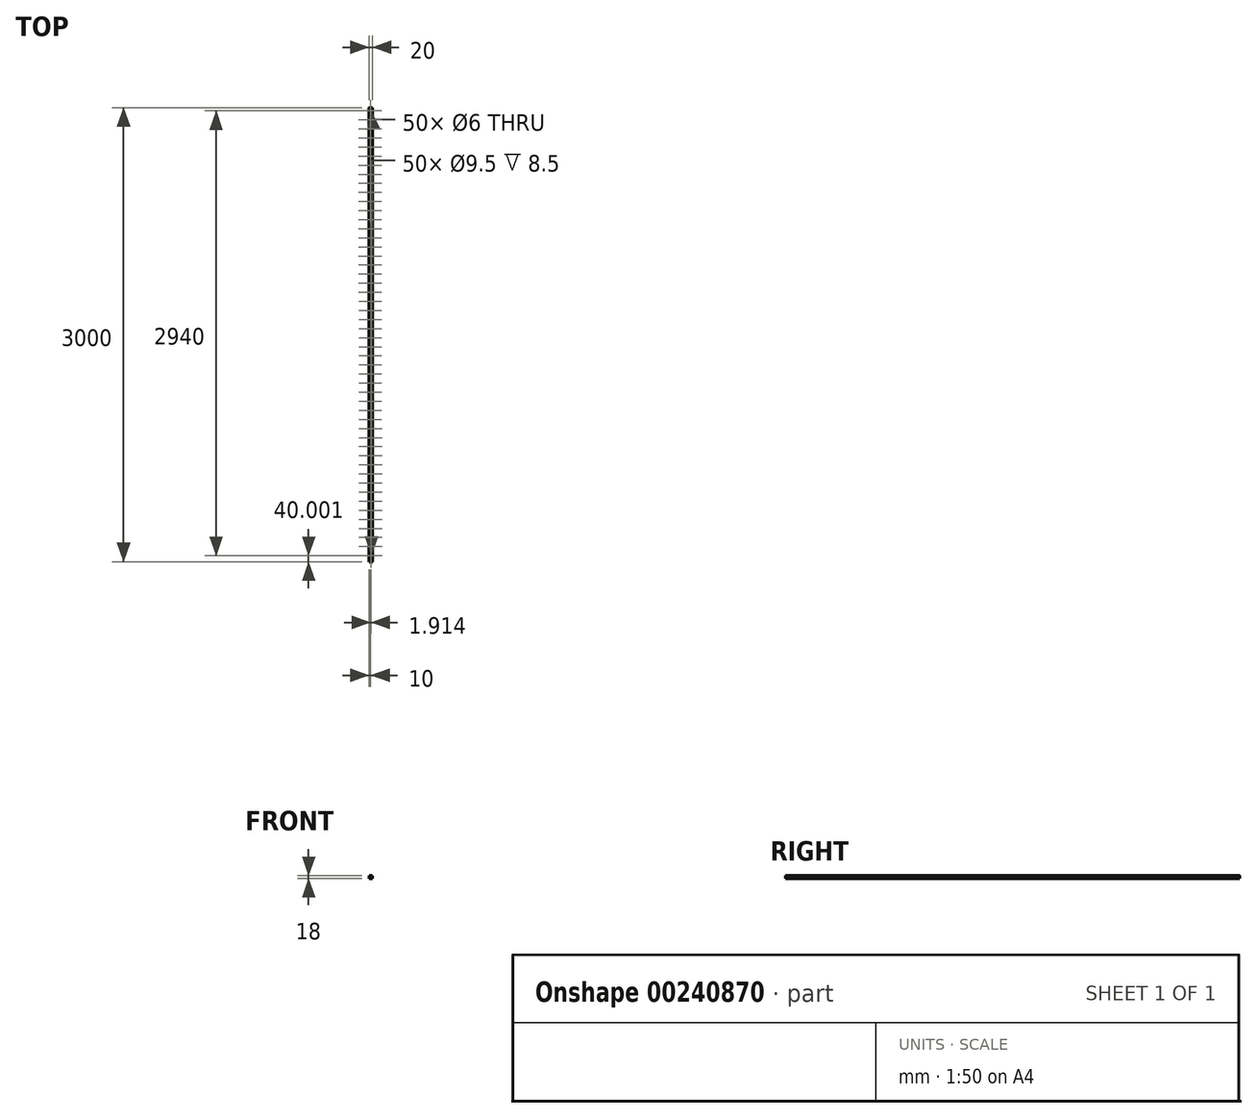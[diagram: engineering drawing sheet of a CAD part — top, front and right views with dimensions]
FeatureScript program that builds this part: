
annotation { "Feature Type Name" : "Feature", "Feature Type Description" : "" }
export const myFeature = defineFeature(function(context is Context, id is Id, definition is map)
    precondition{}
    {
        {
            var Q0;
            Q0=qCreatedBy(makeId("Front.planeOp"),FACE);
            var sketch = newSketch(context, id + "F0", { "sketchPlane" : qUnion([Q0])});
            skLineSegment(sketch, "E0.bottom", {"start": v(-10, 0) * mm, "end": v(10, 0) * mm});
            skLineSegment(sketch, "E0.top", {"start": v(-10, 18) * mm, "end": v(10, 18) * mm});
            skLineSegment(sketch, "E0.left", {"start": v(-10, 0) * mm, "end": v(-10, 18) * mm});
            skLineSegment(sketch, "E0.right", {"start": v(10, 0) * mm, "end": v(10, 18) * mm});
            skLineSegment(sketch, "E1", {"start": v(-18.81, 15) * mm, "end": v(15.35, 15) * mm, "construction": true});
            skCircle(sketch, "E2", {"center": v(-10, 18) * mm, "radius": 2 * mm});
            skCircle(sketch, "E3", {"center": v(10, 18) * mm, "radius": 2 * mm});
            skLineSegment(sketch, "E4.rect.bottom", {"start": v(-2, 0.5) * mm, "end": v(2, 0.5) * mm});
            skLineSegment(sketch, "E4.rect.top", {"start": v(-2, -0.5) * mm, "end": v(2, -0.5) * mm});
            skLineSegment(sketch, "E4.rect.left", {"start": v(-2, 0.5) * mm, "end": v(-2, -0.5) * mm});
            skLineSegment(sketch, "E4.rect.right", {"start": v(2, 0.5) * mm, "end": v(2, -0.5) * mm});
            skPoint(sketch, "E4.rect.middle", {"position": v(0, 0) * mm});
            skCircle(sketch, "E5.MirrorC", {"center": v(-10, 12) * mm, "radius": 2 * mm});
            skCircle(sketch, "E6.MirrorC", {"center": v(10, 12) * mm, "radius": 2 * mm});
            skLineSegment(sketch, "E7", {"start": v(-10, 0.42) * mm, "end": v(-9.58, 0) * mm});
            skLineSegment(sketch, "E8", {"start": v(-13.72, 4) * mm, "end": v(14.81, 4) * mm, "construction": true});
            skLineSegment(sketch, "E9", {"start": v(-12.78, 5.46) * mm, "end": v(14.15, 5.46) * mm, "construction": true});
            skLineSegment(sketch, "E10", {"start": v(-12.88, 2.54) * mm, "end": v(14.15, 2.54) * mm, "construction": true});
            skLineSegment(sketch, "E11", {"start": v(-9.79, 0.21) * mm, "end": v(-10, 0) * mm, "construction": true});
            skLineSegment(sketch, "E12.MirrorCS", {"start": v(10, 0.42) * mm, "end": v(9.58, 0) * mm});
            skCircle(sketch, "E13", {"center": v(-7, 0) * mm, "radius": 0.5 * mm});
            skLineSegment(sketch, "E14", {"start": v(-2, 0.5) * mm, "end": v(-2.5, 0) * mm});
            skLineSegment(sketch, "E15", {"start": v(-2.25, 0.25) * mm, "end": v(-2, 0) * mm, "construction": true});
            skLineSegment(sketch, "E16.MirrorCS", {"start": v(2, 0.5) * mm, "end": v(2.5, 0) * mm});
            skLineSegment(sketch, "E17", {"start": v(-7, 0) * mm, "end": v(-7, 20.38) * mm, "construction": true});
            skLineSegment(sketch, "E18.MirrorCS", {"start": v(7, 0) * mm, "end": v(7, 20.38) * mm, "construction": true});
            skLineSegment(sketch, "E19", {"start": v(-10, 5.46) * mm, "end": v(-7, 8.46) * mm});
            skLineSegment(sketch, "E20", {"start": v(-7, 8.46) * mm, "end": v(-7, 10.93) * mm});
            skLineSegment(sketch, "E21", {"start": v(-7, 10.93) * mm, "end": v(-8.03, 11.65) * mm});
            skLineSegment(sketch, "E22.MirrorCS", {"start": v(10, 5.46) * mm, "end": v(7, 8.46) * mm});
            skLineSegment(sketch, "E23.MirrorCS", {"start": v(7, 8.46) * mm, "end": v(7, 10.93) * mm});
            skLineSegment(sketch, "E24.MirrorCS", {"start": v(7, 10.93) * mm, "end": v(8.03, 11.65) * mm});
            skSolve(sketch);
        }
        {
            var Q0;
            Q0=makeQuery(id+"F0.imprint","IMPRINT",FACE,{"disambiguationData":[TD([[makeQuery(id+"F0.imprint","IMPRINT",EDGE,{"derivedFrom":sQuery(id+"F0.wireOp",EDGE,"E4.rect.bottom")}),1.0]])]});
            extrude(context, id + "F1", {"entities" : qUnion([Q0]), "depth" : 3000 * mm});
        }
        {
            var Q0;
            Q0=makeQuery(id+"F1.opExtrude","SWEPT_FACE",FACE,{"disambiguationData":[OSD([sQuery(id+"F0.wireOp",EDGE,"E0.top")])]});
            var sketch = newSketch(context, id + "F2", { "sketchPlane" : qUnion([Q0])});
            skCircle(sketch, "E25", {"center": v(0, -20) * mm, "radius": 3 * mm});
            skCircle(sketch, "E26", {"center": v(0, -20) * mm, "radius": 4.75 * mm});
            skCircle(sketch, "E27.1.0.0", {"center": v(0.04, -80) * mm, "radius": 3 * mm});
            skCircle(sketch, "E27.1.0.1", {"center": v(0.04, -80) * mm, "radius": 4.75 * mm});
            skLineSegment(sketch, "E27.direction1", {"start": v(0, -20) * mm, "end": v(0.04, -80) * mm});
            skCircle(sketch, "E28.0.2.0", {"center": v(0.08, -140) * mm, "radius": 3 * mm});
            skCircle(sketch, "E28.2.2.0", {"center": v(0.08, -140) * mm, "radius": 4.75 * mm});
            skCircle(sketch, "E28.0.3.0", {"center": v(0.12, -200) * mm, "radius": 3 * mm});
            skCircle(sketch, "E28.2.3.0", {"center": v(0.12, -200) * mm, "radius": 4.75 * mm});
            skCircle(sketch, "E28.0.4.0", {"center": v(0.16, -260) * mm, "radius": 3 * mm});
            skCircle(sketch, "E28.2.4.0", {"center": v(0.16, -260) * mm, "radius": 4.75 * mm});
            skCircle(sketch, "E28.0.5.0", {"center": v(0.2, -320) * mm, "radius": 3 * mm});
            skCircle(sketch, "E28.2.5.0", {"center": v(0.2, -320) * mm, "radius": 4.75 * mm});
            skCircle(sketch, "E28.0.6.0", {"center": v(0.23, -380) * mm, "radius": 3 * mm});
            skCircle(sketch, "E28.2.6.0", {"center": v(0.23, -380) * mm, "radius": 4.75 * mm});
            skCircle(sketch, "E29.0.7.0", {"center": v(0.27, -440) * mm, "radius": 3 * mm});
            skCircle(sketch, "E29.2.7.0", {"center": v(0.27, -440) * mm, "radius": 4.75 * mm});
            skCircle(sketch, "E29.0.8.0", {"center": v(0.31, -500) * mm, "radius": 3 * mm});
            skCircle(sketch, "E29.2.8.0", {"center": v(0.31, -500) * mm, "radius": 4.75 * mm});
            skCircle(sketch, "E29.0.9.0", {"center": v(0.35, -560) * mm, "radius": 3 * mm});
            skCircle(sketch, "E29.2.9.0", {"center": v(0.35, -560) * mm, "radius": 4.75 * mm});
            skCircle(sketch, "E30.0.10.0", {"center": v(0.4, -620) * mm, "radius": 3 * mm});
            skCircle(sketch, "E30.2.10.0", {"center": v(0.4, -620) * mm, "radius": 4.75 * mm});
            skCircle(sketch, "E30.0.11.0", {"center": v(0.43, -680) * mm, "radius": 3 * mm});
            skCircle(sketch, "E30.2.11.0", {"center": v(0.43, -680) * mm, "radius": 4.75 * mm});
            skCircle(sketch, "E30.0.12.0", {"center": v(0.47, -740) * mm, "radius": 3 * mm});
            skCircle(sketch, "E30.2.12.0", {"center": v(0.47, -740) * mm, "radius": 4.75 * mm});
            skCircle(sketch, "E30.0.13.0", {"center": v(0.5, -800) * mm, "radius": 3 * mm});
            skCircle(sketch, "E30.2.13.0", {"center": v(0.5, -800) * mm, "radius": 4.75 * mm});
            skCircle(sketch, "E30.0.14.0", {"center": v(0.55, -860) * mm, "radius": 3 * mm});
            skCircle(sketch, "E30.2.14.0", {"center": v(0.55, -860) * mm, "radius": 4.75 * mm});
            skCircle(sketch, "E30.0.15.0", {"center": v(0.59, -920) * mm, "radius": 3 * mm});
            skCircle(sketch, "E30.2.15.0", {"center": v(0.59, -920) * mm, "radius": 4.75 * mm});
            skCircle(sketch, "E30.0.16.0", {"center": v(0.62, -980) * mm, "radius": 3 * mm});
            skCircle(sketch, "E30.2.16.0", {"center": v(0.62, -980) * mm, "radius": 4.75 * mm});
            skCircle(sketch, "E30.0.17.0", {"center": v(0.66, -1040) * mm, "radius": 3 * mm});
            skCircle(sketch, "E30.2.17.0", {"center": v(0.66, -1040) * mm, "radius": 4.75 * mm});
            skCircle(sketch, "E30.0.18.0", {"center": v(0.7, -1100) * mm, "radius": 3 * mm});
            skCircle(sketch, "E30.2.18.0", {"center": v(0.7, -1100) * mm, "radius": 4.75 * mm});
            skCircle(sketch, "E30.0.19.0", {"center": v(0.74, -1160) * mm, "radius": 3 * mm});
            skCircle(sketch, "E30.2.19.0", {"center": v(0.74, -1160) * mm, "radius": 4.75 * mm});
            skCircle(sketch, "E30.0.20.0", {"center": v(0.78, -1220) * mm, "radius": 3 * mm});
            skCircle(sketch, "E30.2.20.0", {"center": v(0.78, -1220) * mm, "radius": 4.75 * mm});
            skCircle(sketch, "E30.0.21.0", {"center": v(0.82, -1280) * mm, "radius": 3 * mm});
            skCircle(sketch, "E30.2.21.0", {"center": v(0.82, -1280) * mm, "radius": 4.75 * mm});
            skCircle(sketch, "E31.0.22.0", {"center": v(0.86, -1340) * mm, "radius": 3 * mm});
            skCircle(sketch, "E31.2.22.0", {"center": v(0.86, -1340) * mm, "radius": 4.75 * mm});
            skCircle(sketch, "E31.0.23.0", {"center": v(0.9, -1400) * mm, "radius": 3 * mm});
            skCircle(sketch, "E31.2.23.0", {"center": v(0.9, -1400) * mm, "radius": 4.75 * mm});
            skCircle(sketch, "E32.0.24.0", {"center": v(0.94, -1460) * mm, "radius": 3 * mm});
            skCircle(sketch, "E32.2.24.0", {"center": v(0.94, -1460) * mm, "radius": 4.75 * mm});
            skCircle(sketch, "E33.0.25.0", {"center": v(0.98, -1520) * mm, "radius": 3 * mm});
            skCircle(sketch, "E33.2.25.0", {"center": v(0.98, -1520) * mm, "radius": 4.75 * mm});
            skCircle(sketch, "E33.0.26.0", {"center": v(1.02, -1580) * mm, "radius": 3 * mm});
            skCircle(sketch, "E33.2.26.0", {"center": v(1.02, -1580) * mm, "radius": 4.75 * mm});
            skCircle(sketch, "E33.0.27.0", {"center": v(1.05, -1640) * mm, "radius": 3 * mm});
            skCircle(sketch, "E33.2.27.0", {"center": v(1.05, -1640) * mm, "radius": 4.75 * mm});
            skCircle(sketch, "E33.0.28.0", {"center": v(1.1, -1700) * mm, "radius": 3 * mm});
            skCircle(sketch, "E33.2.28.0", {"center": v(1.1, -1700) * mm, "radius": 4.75 * mm});
            skCircle(sketch, "E33.0.29.0", {"center": v(1.13, -1760) * mm, "radius": 3 * mm});
            skCircle(sketch, "E33.2.29.0", {"center": v(1.13, -1760) * mm, "radius": 4.75 * mm});
            skCircle(sketch, "E33.0.30.0", {"center": v(1.17, -1820) * mm, "radius": 3 * mm});
            skCircle(sketch, "E33.2.30.0", {"center": v(1.17, -1820) * mm, "radius": 4.75 * mm});
            skCircle(sketch, "E33.0.31.0", {"center": v(1.21, -1880) * mm, "radius": 3 * mm});
            skCircle(sketch, "E33.2.31.0", {"center": v(1.21, -1880) * mm, "radius": 4.75 * mm});
            skCircle(sketch, "E33.0.32.0", {"center": v(1.25, -1940) * mm, "radius": 3 * mm});
            skCircle(sketch, "E33.2.32.0", {"center": v(1.25, -1940) * mm, "radius": 4.75 * mm});
            skCircle(sketch, "E33.0.33.0", {"center": v(1.29, -2000) * mm, "radius": 3 * mm});
            skCircle(sketch, "E33.2.33.0", {"center": v(1.29, -2000) * mm, "radius": 4.75 * mm});
            skCircle(sketch, "E33.0.34.0", {"center": v(1.33, -2060) * mm, "radius": 3 * mm});
            skCircle(sketch, "E33.2.34.0", {"center": v(1.33, -2060) * mm, "radius": 4.75 * mm});
            skCircle(sketch, "E33.0.35.0", {"center": v(1.37, -2120) * mm, "radius": 3 * mm});
            skCircle(sketch, "E33.2.35.0", {"center": v(1.37, -2120) * mm, "radius": 4.75 * mm});
            skCircle(sketch, "E33.0.36.0", {"center": v(1.4, -2180) * mm, "radius": 3 * mm});
            skCircle(sketch, "E33.2.36.0", {"center": v(1.4, -2180) * mm, "radius": 4.75 * mm});
            skCircle(sketch, "E33.0.37.0", {"center": v(1.45, -2240) * mm, "radius": 3 * mm});
            skCircle(sketch, "E33.2.37.0", {"center": v(1.45, -2240) * mm, "radius": 4.75 * mm});
            skCircle(sketch, "E33.0.38.0", {"center": v(1.48, -2300) * mm, "radius": 3 * mm});
            skCircle(sketch, "E33.2.38.0", {"center": v(1.48, -2300) * mm, "radius": 4.75 * mm});
            skCircle(sketch, "E33.0.39.0", {"center": v(1.52, -2360) * mm, "radius": 3 * mm});
            skCircle(sketch, "E33.2.39.0", {"center": v(1.52, -2360) * mm, "radius": 4.75 * mm});
            skCircle(sketch, "E33.0.40.0", {"center": v(1.56, -2420) * mm, "radius": 3 * mm});
            skCircle(sketch, "E33.2.40.0", {"center": v(1.56, -2420) * mm, "radius": 4.75 * mm});
            skCircle(sketch, "E33.0.41.0", {"center": v(1.6, -2480) * mm, "radius": 3 * mm});
            skCircle(sketch, "E33.2.41.0", {"center": v(1.6, -2480) * mm, "radius": 4.75 * mm});
            skCircle(sketch, "E33.0.42.0", {"center": v(1.64, -2540) * mm, "radius": 3 * mm});
            skCircle(sketch, "E33.2.42.0", {"center": v(1.64, -2540) * mm, "radius": 4.75 * mm});
            skCircle(sketch, "E33.0.43.0", {"center": v(1.68, -2600) * mm, "radius": 3 * mm});
            skCircle(sketch, "E33.2.43.0", {"center": v(1.68, -2600) * mm, "radius": 4.75 * mm});
            skCircle(sketch, "E33.0.44.0", {"center": v(1.72, -2660) * mm, "radius": 3 * mm});
            skCircle(sketch, "E33.2.44.0", {"center": v(1.72, -2660) * mm, "radius": 4.75 * mm});
            skCircle(sketch, "E33.0.45.0", {"center": v(1.76, -2720) * mm, "radius": 3 * mm});
            skCircle(sketch, "E33.2.45.0", {"center": v(1.76, -2720) * mm, "radius": 4.75 * mm});
            skCircle(sketch, "E33.0.46.0", {"center": v(1.8, -2780) * mm, "radius": 3 * mm});
            skCircle(sketch, "E33.2.46.0", {"center": v(1.8, -2780) * mm, "radius": 4.75 * mm});
            skCircle(sketch, "E33.0.47.0", {"center": v(1.84, -2840) * mm, "radius": 3 * mm});
            skCircle(sketch, "E33.2.47.0", {"center": v(1.84, -2840) * mm, "radius": 4.75 * mm});
            skCircle(sketch, "E33.0.48.0", {"center": v(1.87, -2900) * mm, "radius": 3 * mm});
            skCircle(sketch, "E33.2.48.0", {"center": v(1.87, -2900) * mm, "radius": 4.75 * mm});
            skCircle(sketch, "E33.0.49.0", {"center": v(1.91, -2960) * mm, "radius": 3 * mm});
            skCircle(sketch, "E33.2.49.0", {"center": v(1.91, -2960) * mm, "radius": 4.75 * mm});
            skSolve(sketch);
        }
        {
            var Q0;
            Q0=makeQuery(id+"F2.imprint","IMPRINT",FACE,{"disambiguationData":[TD([[makeQuery(id+"F2.imprint","IMPRINT",EDGE,{"derivedFrom":sQuery(id+"F2.wireOp",EDGE,"E25")}),1.0]])]});
            var Q1;
            Q1=makeQuery(id+"F2.imprint","IMPRINT",FACE,{"disambiguationData":[TD([[makeQuery(id+"F2.imprint","IMPRINT",EDGE,{"derivedFrom":sQuery(id+"F2.wireOp",EDGE,"E27.1.0.0")}),1.0]])]});
            var Q2;
            Q2=makeQuery(id+"F2.imprint","IMPRINT",FACE,{"disambiguationData":[TD([[makeQuery(id+"F2.imprint","IMPRINT",EDGE,{"derivedFrom":sQuery(id+"F2.wireOp",EDGE,"E28.0.2.0")}),1.0]])]});
            var Q3;
            Q3=makeQuery(id+"F2.imprint","IMPRINT",FACE,{"disambiguationData":[TD([[makeQuery(id+"F2.imprint","IMPRINT",EDGE,{"derivedFrom":sQuery(id+"F2.wireOp",EDGE,"E28.0.3.0")}),1.0]])]});
            var Q4;
            Q4=makeQuery(id+"F2.imprint","IMPRINT",FACE,{"disambiguationData":[TD([[makeQuery(id+"F2.imprint","IMPRINT",EDGE,{"derivedFrom":sQuery(id+"F2.wireOp",EDGE,"E28.0.4.0")}),1.0]])]});
            var Q5;
            Q5=makeQuery(id+"F2.imprint","IMPRINT",FACE,{"disambiguationData":[TD([[makeQuery(id+"F2.imprint","IMPRINT",EDGE,{"derivedFrom":sQuery(id+"F2.wireOp",EDGE,"E28.0.5.0")}),1.0]])]});
            var Q6;
            Q6=makeQuery(id+"F2.imprint","IMPRINT",FACE,{"disambiguationData":[TD([[makeQuery(id+"F2.imprint","IMPRINT",EDGE,{"derivedFrom":sQuery(id+"F2.wireOp",EDGE,"E28.0.6.0")}),1.0]])]});
            var Q7;
            Q7=makeQuery(id+"F2.imprint","IMPRINT",FACE,{"disambiguationData":[TD([[makeQuery(id+"F2.imprint","IMPRINT",EDGE,{"derivedFrom":sQuery(id+"F2.wireOp",EDGE,"E29.0.7.0")}),1.0]])]});
            var Q8;
            Q8=makeQuery(id+"F2.imprint","IMPRINT",FACE,{"disambiguationData":[TD([[makeQuery(id+"F2.imprint","IMPRINT",EDGE,{"derivedFrom":sQuery(id+"F2.wireOp",EDGE,"E29.0.8.0")}),1.0]])]});
            var Q9;
            Q9=makeQuery(id+"F2.imprint","IMPRINT",FACE,{"disambiguationData":[TD([[makeQuery(id+"F2.imprint","IMPRINT",EDGE,{"derivedFrom":sQuery(id+"F2.wireOp",EDGE,"E29.0.9.0")}),1.0]])]});
            var Q10;
            Q10=makeQuery(id+"F2.imprint","IMPRINT",FACE,{"disambiguationData":[TD([[makeQuery(id+"F2.imprint","IMPRINT",EDGE,{"derivedFrom":sQuery(id+"F2.wireOp",EDGE,"E31.0.23.0")}),1.0]])]});
            var Q11;
            Q11=makeQuery(id+"F2.imprint","IMPRINT",FACE,{"disambiguationData":[TD([[makeQuery(id+"F2.imprint","IMPRINT",EDGE,{"derivedFrom":sQuery(id+"F2.wireOp",EDGE,"E31.0.22.0")}),1.0]])]});
            var Q12;
            Q12=makeQuery(id+"F2.imprint","IMPRINT",FACE,{"disambiguationData":[TD([[makeQuery(id+"F2.imprint","IMPRINT",EDGE,{"derivedFrom":sQuery(id+"F2.wireOp",EDGE,"E30.0.21.0")}),1.0]])]});
            var Q13;
            Q13=makeQuery(id+"F2.imprint","IMPRINT",FACE,{"disambiguationData":[TD([[makeQuery(id+"F2.imprint","IMPRINT",EDGE,{"derivedFrom":sQuery(id+"F2.wireOp",EDGE,"E30.0.20.0")}),1.0]])]});
            var Q14;
            Q14=makeQuery(id+"F2.imprint","IMPRINT",FACE,{"disambiguationData":[TD([[makeQuery(id+"F2.imprint","IMPRINT",EDGE,{"derivedFrom":sQuery(id+"F2.wireOp",EDGE,"E30.0.19.0")}),1.0]])]});
            var Q15;
            Q15=makeQuery(id+"F2.imprint","IMPRINT",FACE,{"disambiguationData":[TD([[makeQuery(id+"F2.imprint","IMPRINT",EDGE,{"derivedFrom":sQuery(id+"F2.wireOp",EDGE,"E30.0.18.0")}),1.0]])]});
            var Q16;
            Q16=makeQuery(id+"F2.imprint","IMPRINT",FACE,{"disambiguationData":[TD([[makeQuery(id+"F2.imprint","IMPRINT",EDGE,{"derivedFrom":sQuery(id+"F2.wireOp",EDGE,"E30.0.17.0")}),1.0]])]});
            var Q17;
            Q17=makeQuery(id+"F2.imprint","IMPRINT",FACE,{"disambiguationData":[TD([[makeQuery(id+"F2.imprint","IMPRINT",EDGE,{"derivedFrom":sQuery(id+"F2.wireOp",EDGE,"E30.0.16.0")}),1.0]])]});
            var Q18;
            Q18=makeQuery(id+"F2.imprint","IMPRINT",FACE,{"disambiguationData":[TD([[makeQuery(id+"F2.imprint","IMPRINT",EDGE,{"derivedFrom":sQuery(id+"F2.wireOp",EDGE,"E30.0.15.0")}),1.0]])]});
            var Q19;
            Q19=makeQuery(id+"F2.imprint","IMPRINT",FACE,{"disambiguationData":[TD([[makeQuery(id+"F2.imprint","IMPRINT",EDGE,{"derivedFrom":sQuery(id+"F2.wireOp",EDGE,"E30.0.14.0")}),1.0]])]});
            var Q20;
            Q20=makeQuery(id+"F2.imprint","IMPRINT",FACE,{"disambiguationData":[TD([[makeQuery(id+"F2.imprint","IMPRINT",EDGE,{"derivedFrom":sQuery(id+"F2.wireOp",EDGE,"E30.0.13.0")}),1.0]])]});
            var Q21;
            Q21=makeQuery(id+"F2.imprint","IMPRINT",FACE,{"disambiguationData":[TD([[makeQuery(id+"F2.imprint","IMPRINT",EDGE,{"derivedFrom":sQuery(id+"F2.wireOp",EDGE,"E30.0.12.0")}),1.0]])]});
            var Q22;
            Q22=makeQuery(id+"F2.imprint","IMPRINT",FACE,{"disambiguationData":[TD([[makeQuery(id+"F2.imprint","IMPRINT",EDGE,{"derivedFrom":sQuery(id+"F2.wireOp",EDGE,"E30.0.11.0")}),1.0]])]});
            var Q23;
            Q23=makeQuery(id+"F2.imprint","IMPRINT",FACE,{"disambiguationData":[TD([[makeQuery(id+"F2.imprint","IMPRINT",EDGE,{"derivedFrom":sQuery(id+"F2.wireOp",EDGE,"E30.0.10.0")}),1.0]])]});
            var Q24;
            Q24=makeQuery(id+"F2.imprint","IMPRINT",FACE,{"disambiguationData":[TD([[makeQuery(id+"F2.imprint","IMPRINT",EDGE,{"derivedFrom":sQuery(id+"F2.wireOp",EDGE,"E32.0.24.0")}),1.0]])]});
            var Q25;
            Q25=makeQuery(id+"F2.imprint","IMPRINT",FACE,{"disambiguationData":[TD([[makeQuery(id+"F2.imprint","IMPRINT",EDGE,{"derivedFrom":sQuery(id+"F2.wireOp",EDGE,"E33.0.25.0")}),1.0]])]});
            var Q26;
            Q26=makeQuery(id+"F2.imprint","IMPRINT",FACE,{"disambiguationData":[TD([[makeQuery(id+"F2.imprint","IMPRINT",EDGE,{"derivedFrom":sQuery(id+"F2.wireOp",EDGE,"E33.0.26.0")}),1.0]])]});
            var Q27;
            Q27=makeQuery(id+"F2.imprint","IMPRINT",FACE,{"disambiguationData":[TD([[makeQuery(id+"F2.imprint","IMPRINT",EDGE,{"derivedFrom":sQuery(id+"F2.wireOp",EDGE,"E33.0.27.0")}),1.0]])]});
            var Q28;
            Q28=makeQuery(id+"F2.imprint","IMPRINT",FACE,{"disambiguationData":[TD([[makeQuery(id+"F2.imprint","IMPRINT",EDGE,{"derivedFrom":sQuery(id+"F2.wireOp",EDGE,"E33.0.28.0")}),1.0]])]});
            var Q29;
            Q29=makeQuery(id+"F2.imprint","IMPRINT",FACE,{"disambiguationData":[TD([[makeQuery(id+"F2.imprint","IMPRINT",EDGE,{"derivedFrom":sQuery(id+"F2.wireOp",EDGE,"E33.0.29.0")}),1.0]])]});
            var Q30;
            Q30=makeQuery(id+"F2.imprint","IMPRINT",FACE,{"disambiguationData":[TD([[makeQuery(id+"F2.imprint","IMPRINT",EDGE,{"derivedFrom":sQuery(id+"F2.wireOp",EDGE,"E33.0.30.0")}),1.0]])]});
            var Q31;
            Q31=makeQuery(id+"F2.imprint","IMPRINT",FACE,{"disambiguationData":[TD([[makeQuery(id+"F2.imprint","IMPRINT",EDGE,{"derivedFrom":sQuery(id+"F2.wireOp",EDGE,"E33.0.31.0")}),1.0]])]});
            var Q32;
            Q32=makeQuery(id+"F2.imprint","IMPRINT",FACE,{"disambiguationData":[TD([[makeQuery(id+"F2.imprint","IMPRINT",EDGE,{"derivedFrom":sQuery(id+"F2.wireOp",EDGE,"E33.0.32.0")}),1.0]])]});
            var Q33;
            Q33=makeQuery(id+"F2.imprint","IMPRINT",FACE,{"disambiguationData":[TD([[makeQuery(id+"F2.imprint","IMPRINT",EDGE,{"derivedFrom":sQuery(id+"F2.wireOp",EDGE,"E33.0.33.0")}),1.0]])]});
            var Q34;
            Q34=makeQuery(id+"F2.imprint","IMPRINT",FACE,{"disambiguationData":[TD([[makeQuery(id+"F2.imprint","IMPRINT",EDGE,{"derivedFrom":sQuery(id+"F2.wireOp",EDGE,"E33.0.34.0")}),1.0]])]});
            var Q35;
            Q35=makeQuery(id+"F2.imprint","IMPRINT",FACE,{"disambiguationData":[TD([[makeQuery(id+"F2.imprint","IMPRINT",EDGE,{"derivedFrom":sQuery(id+"F2.wireOp",EDGE,"E33.0.35.0")}),1.0]])]});
            var Q36;
            Q36=makeQuery(id+"F2.imprint","IMPRINT",FACE,{"disambiguationData":[TD([[makeQuery(id+"F2.imprint","IMPRINT",EDGE,{"derivedFrom":sQuery(id+"F2.wireOp",EDGE,"E33.0.36.0")}),1.0]])]});
            var Q37;
            Q37=makeQuery(id+"F2.imprint","IMPRINT",FACE,{"disambiguationData":[TD([[makeQuery(id+"F2.imprint","IMPRINT",EDGE,{"derivedFrom":sQuery(id+"F2.wireOp",EDGE,"E33.0.37.0")}),1.0]])]});
            var Q38;
            Q38=makeQuery(id+"F2.imprint","IMPRINT",FACE,{"disambiguationData":[TD([[makeQuery(id+"F2.imprint","IMPRINT",EDGE,{"derivedFrom":sQuery(id+"F2.wireOp",EDGE,"E33.0.38.0")}),1.0]])]});
            var Q39;
            Q39=makeQuery(id+"F2.imprint","IMPRINT",FACE,{"disambiguationData":[TD([[makeQuery(id+"F2.imprint","IMPRINT",EDGE,{"derivedFrom":sQuery(id+"F2.wireOp",EDGE,"E33.0.39.0")}),1.0]])]});
            var Q40;
            Q40=makeQuery(id+"F2.imprint","IMPRINT",FACE,{"disambiguationData":[TD([[makeQuery(id+"F2.imprint","IMPRINT",EDGE,{"derivedFrom":sQuery(id+"F2.wireOp",EDGE,"E33.0.40.0")}),1.0]])]});
            var Q41;
            Q41=makeQuery(id+"F2.imprint","IMPRINT",FACE,{"disambiguationData":[TD([[makeQuery(id+"F2.imprint","IMPRINT",EDGE,{"derivedFrom":sQuery(id+"F2.wireOp",EDGE,"E33.0.41.0")}),1.0]])]});
            var Q42;
            Q42=makeQuery(id+"F2.imprint","IMPRINT",FACE,{"disambiguationData":[TD([[makeQuery(id+"F2.imprint","IMPRINT",EDGE,{"derivedFrom":sQuery(id+"F2.wireOp",EDGE,"E33.0.42.0")}),1.0]])]});
            var Q43;
            Q43=makeQuery(id+"F2.imprint","IMPRINT",FACE,{"disambiguationData":[TD([[makeQuery(id+"F2.imprint","IMPRINT",EDGE,{"derivedFrom":sQuery(id+"F2.wireOp",EDGE,"E33.0.43.0")}),1.0]])]});
            var Q44;
            Q44=makeQuery(id+"F2.imprint","IMPRINT",FACE,{"disambiguationData":[TD([[makeQuery(id+"F2.imprint","IMPRINT",EDGE,{"derivedFrom":sQuery(id+"F2.wireOp",EDGE,"E33.0.44.0")}),1.0]])]});
            var Q45;
            Q45=makeQuery(id+"F2.imprint","IMPRINT",FACE,{"disambiguationData":[TD([[makeQuery(id+"F2.imprint","IMPRINT",EDGE,{"derivedFrom":sQuery(id+"F2.wireOp",EDGE,"E33.0.45.0")}),1.0]])]});
            var Q46;
            Q46=makeQuery(id+"F2.imprint","IMPRINT",FACE,{"disambiguationData":[TD([[makeQuery(id+"F2.imprint","IMPRINT",EDGE,{"derivedFrom":sQuery(id+"F2.wireOp",EDGE,"E33.0.46.0")}),1.0]])]});
            var Q47;
            Q47=makeQuery(id+"F2.imprint","IMPRINT",FACE,{"disambiguationData":[TD([[makeQuery(id+"F2.imprint","IMPRINT",EDGE,{"derivedFrom":sQuery(id+"F2.wireOp",EDGE,"E33.0.49.0")}),1.0]])]});
            var Q48;
            Q48=makeQuery(id+"F2.imprint","IMPRINT",FACE,{"disambiguationData":[TD([[makeQuery(id+"F2.imprint","IMPRINT",EDGE,{"derivedFrom":sQuery(id+"F2.wireOp",EDGE,"E33.0.48.0")}),1.0]])]});
            var Q49;
            Q49=makeQuery(id+"F2.imprint","IMPRINT",FACE,{"disambiguationData":[TD([[makeQuery(id+"F2.imprint","IMPRINT",EDGE,{"derivedFrom":sQuery(id+"F2.wireOp",EDGE,"E33.0.47.0")}),1.0]])]});
            var Q50;
            Q50=sQuery(id+"F2.wireOp",EDGE,"E25");
            extrude(context, id + "F3", {"entities" : qUnion([Q0, Q1, Q2, Q3, Q4, Q5, Q6, Q7, Q8, Q9, Q10, Q11, Q12, Q13, Q14, Q15, Q16, Q17, Q18, Q19, Q20, Q21, Q22, Q23, Q24, Q25, Q26, Q27, Q28, Q29, Q30, Q31, Q32, Q33, Q34, Q35, Q36, Q37, Q38, Q39, Q40, Q41, Q42, Q43, Q44, Q45, Q46, Q47, Q48, Q49]), "operationType" : NewBodyOperationType.REMOVE, "surfaceEntities" : qUnion([Q50]), "endBound" : BoundingType.THROUGH_ALL, "oppositeDirection" : true, "depth" : 25 * mm});
        }
        {
            var Q0;
            Q0=qSketchRegion(id+"F2",true);
            extrude(context, id + "F4", {"entities" : qUnion([Q0]), "operationType" : NewBodyOperationType.REMOVE, "oppositeDirection" : true, "depth" : 8.5 * mm});
        }
    });
